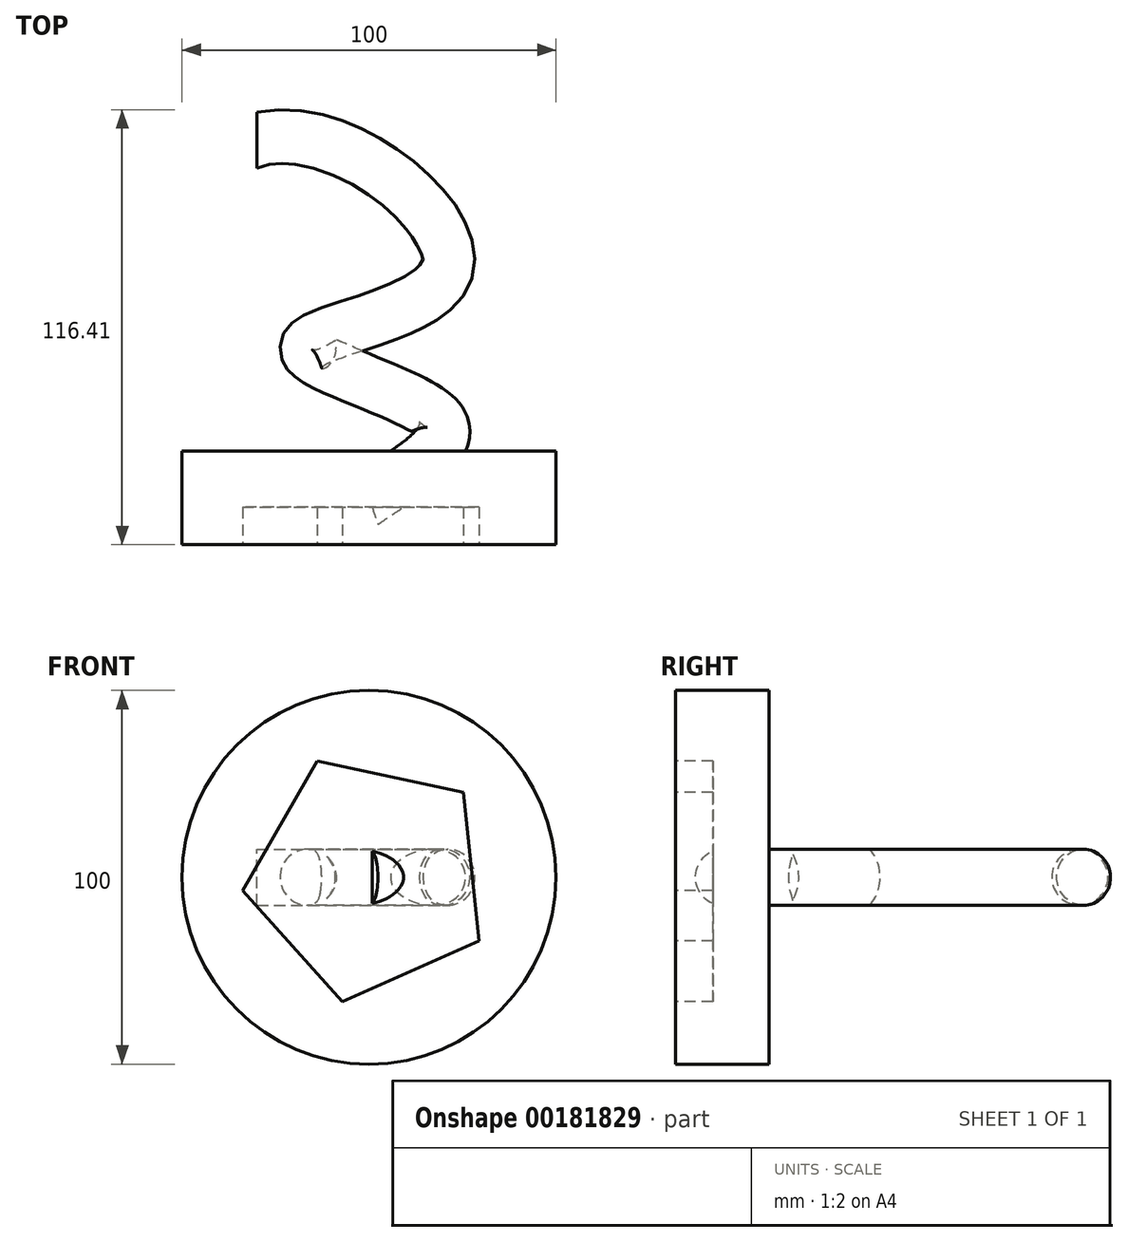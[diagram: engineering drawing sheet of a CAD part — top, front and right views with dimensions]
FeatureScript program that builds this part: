
annotation { "Feature Type Name" : "Feature", "Feature Type Description" : "" }
export const myFeature = defineFeature(function(context is Context, id is Id, definition is map)
    precondition{}
    {
        {
            var Q0;
            Q0=qCreatedBy(makeId("Front.planeOp"),FACE);
            var sketch = newSketch(context, id + "F0", { "sketchPlane" : qUnion([Q0])});
            skCircle(sketch, "E0", {"center": v(0, 0) * mm, "radius": 50 * mm});
            skSolve(sketch);
        }
        {
            var Q0;
            Q0=makeQuery(id+"F0.imprint","IMPRINT",FACE,{"disambiguationData":[TD([[makeQuery(id+"F0.imprint","IMPRINT",EDGE,{"derivedFrom":sQuery(id+"F0.wireOp",EDGE,"E0")}),1.0]])]});
            extrude(context, id + "F1", {"entities" : qUnion([Q0]), "endBound" : BoundingType.SYMMETRIC, "depth" : 25 * mm});
        }
        {
            var Q0;
            Q0=makeQuery(id+"F1.opExtrude","CAP_FACE",FACE,{"disambiguationData":[OSD([sQuery(id+"F0.wireOp",EDGE,"E0")])],"isStart":false});
            var sketch = newSketch(context, id + "F2", { "sketchPlane" : qUnion([Q0])});
            skLineSegment(sketch, "E1", {"start": v(78.41, -45.27) * mm, "end": v(-61.8, 35.68) * mm, "construction": true});
            skCircle(sketch, "E2.cCircle", {"center": v(0, 0) * mm, "radius": 27.53 * mm, "construction": true});
            skLineSegment(sketch, "E2.0", {"start": v(29.47, -17.01) * mm, "end": v(-7.07, -33.28) * mm});
            skLineSegment(sketch, "E2.1", {"start": v(-7.07, -33.28) * mm, "end": v(-33.84, -3.56) * mm});
            skLineSegment(sketch, "E2.2", {"start": v(-33.84, -3.56) * mm, "end": v(-13.84, 31.08) * mm});
            skLineSegment(sketch, "E2.3", {"start": v(-13.84, 31.08) * mm, "end": v(25.29, 22.77) * mm});
            skLineSegment(sketch, "E2.4", {"start": v(25.29, 22.77) * mm, "end": v(29.47, -17.01) * mm});
            skPoint(sketch, "E2.0.midPoint", {"position": v(11.2, -25.15) * mm});
            skSolve(sketch);
        }
        {
            var Q0;
            Q0 = qSketchRegion(id + "F2", true);
            extrude(context, id + "F3", {"entities" : qUnion([Q0]), "operationType" : NewBodyOperationType.REMOVE, "oppositeDirection" : true, "depth" : 10 * mm});
        }
        {
            var Q0;
            Q0=qCreatedBy(makeId("Top.planeOp"),FACE);
            var sketch = newSketch(context, id + "F4", { "sketchPlane" : qUnion([Q0])});
            skFitSpline(sketch, "E3", {"points": [v(0, 0) * mm, v(18.86, 20.22) * mm, v(-16.37, 40) * mm, v(20.34, 60.22) * mm, v(-30, 95.7) * mm], "startDerivative": vector(145.9, 101.12) * mm, "endDerivative": vector(-220.35, -63.4) * mm});
            skSolve(sketch);
        }
        {
            var Q0;
            Q0=sQuery(id+"F4.wireOp",VERTEX,"E3.4.internal");
            var Q1;
            Q1=qCreatedBy(makeId("Right.planeOp"),FACE);
            cPlane(context, id + "F5", {"entities" : qUnion([Q0, Q1]), "cplaneType" : CPlaneType.PLANE_POINT, "offset" : 25 * mm, "width" : 150 * mm, "height" : 150 * mm});
        }
        {
            var Q0;
            Q0=qCreatedBy(id+"F5.planeOp",FACE);
            var sketch = newSketch(context, id + "F6", { "sketchPlane" : qUnion([Q0])});
            skCircle(sketch, "E4", {"center": v(95.7, 0) * mm, "radius": 7.5 * mm});
            skSolve(sketch);
        }
        {
            var Q0;
            Q0=makeQuery(id+"F6.imprint","IMPRINT",FACE,{"disambiguationData":[TD([[makeQuery(id+"F6.imprint","IMPRINT",EDGE,{"derivedFrom":sQuery(id+"F6.wireOp",EDGE,"E4")}),1.0]])]});
            var Q1;
            Q1=sQuery(id+"F4.wireOp",EDGE,"E3");
            sweep(context, id + "F7", {"operationType" : NewBodyOperationType.ADD, "profiles" : qUnion([Q0]), "path" : qUnion([Q1])});
        }
    });
